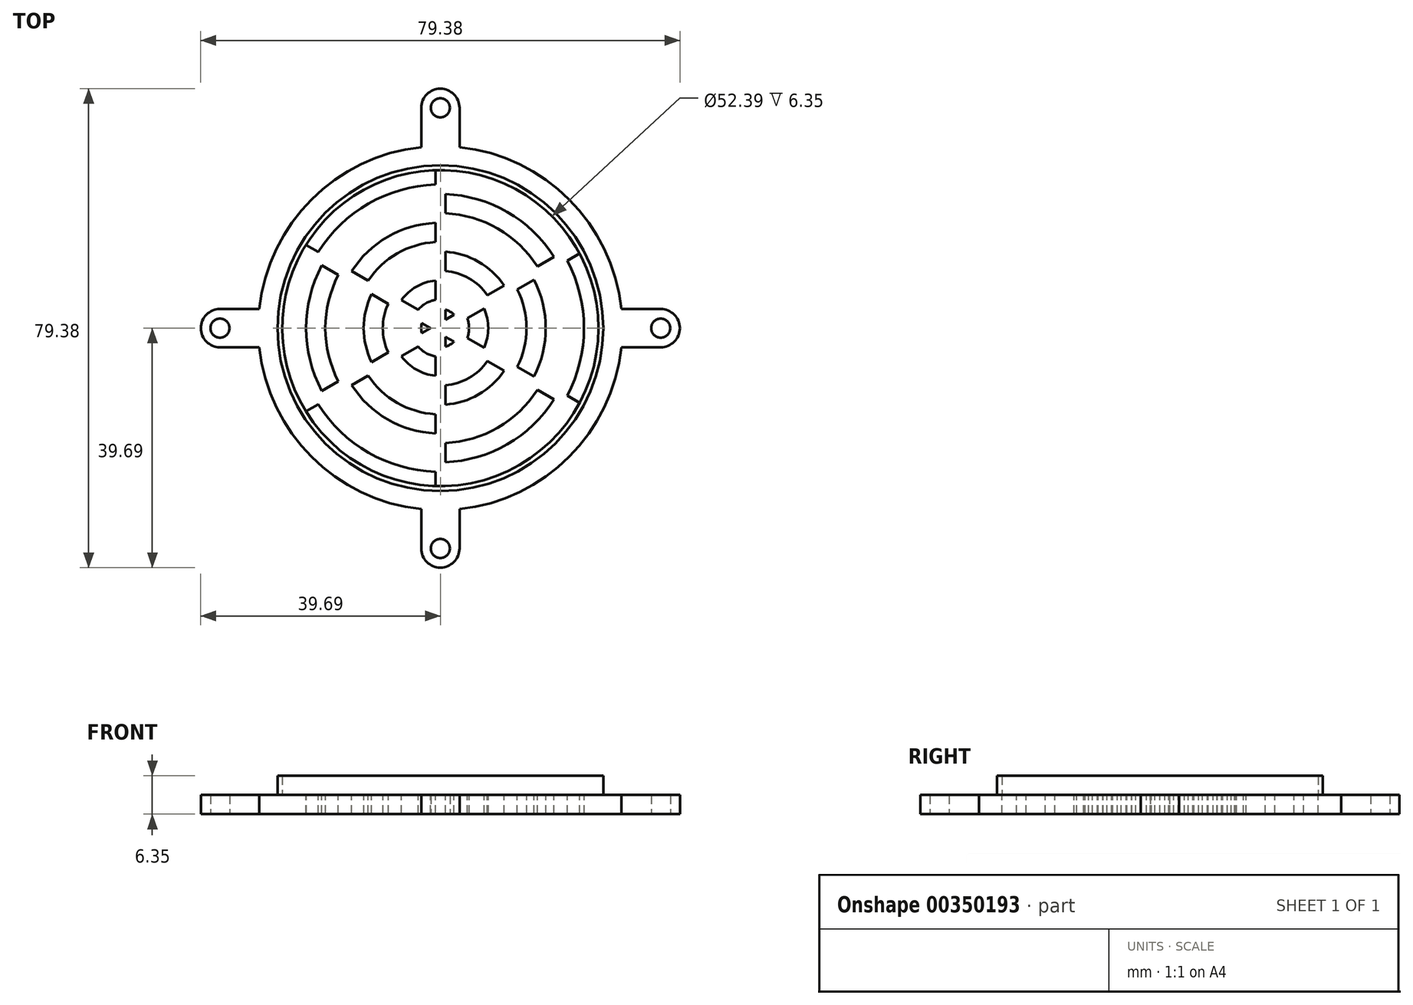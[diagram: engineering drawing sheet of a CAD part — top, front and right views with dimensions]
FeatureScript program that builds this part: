
annotation { "Feature Type Name" : "Feature", "Feature Type Description" : "" }
export const myFeature = defineFeature(function(context is Context, id is Id, definition is map)
    precondition{}
    {
        {
            var Q0;
            Q0=qCreatedBy(makeId("Top.planeOp"),FACE);
            var sketch = newSketch(context, id + "F0", { "sketchPlane" : qUnion([Q0])});
            skArc(sketch, "E0", {"start": v(30, 3.17) * mm, "mid": v(21.33, 21.33) * mm, "end": v(3.17, 30) * mm});
            skLineSegment(sketch, "E1.0", {"start": v(36.51, 3.18) * mm, "end": v(30, 3.17) * mm});
            skLineSegment(sketch, "E2.0", {"start": v(36.51, -3.17) * mm, "end": v(30, -3.17) * mm});
            skLineSegment(sketch, "E3.trimOffspring", {"start": v(-30, 3.17) * mm, "end": v(-30.16, 3.17) * mm});
            skArc(sketch, "E4", {"start": v(36.51, -3.17) * mm, "mid": v(39.69, 0) * mm, "end": v(36.51, 3.17) * mm});
            skCircle(sketch, "E5", {"center": v(36.51, 0) * mm, "radius": 1.59 * mm});
            skPoint(sketch, "E6.orphan", {"position": v(30.16, 0) * mm});
            skLineSegment(sketch, "E7.trimOffspring", {"start": v(-30, -3.18) * mm, "end": v(-30.16, -3.18) * mm});
            skLineSegment(sketch, "E8.1.0", {"start": v(-3.17, 36.51) * mm, "end": v(-3.17, 30) * mm});
            skArc(sketch, "E8.1.1", {"start": v(3.17, 36.51) * mm, "mid": v(0, 39.69) * mm, "end": v(-3.17, 36.51) * mm});
            skLineSegment(sketch, "E8.1.2", {"start": v(3.17, 36.51) * mm, "end": v(3.17, 30) * mm});
            skCircle(sketch, "E8.1.3", {"center": v(0, 36.51) * mm, "radius": 1.59 * mm});
            skLineSegment(sketch, "E8.2.0", {"start": v(-36.51, -3.17) * mm, "end": v(-30, -3.17) * mm});
            skArc(sketch, "E8.2.1", {"start": v(-36.51, 3.17) * mm, "mid": v(-39.69, 0) * mm, "end": v(-36.51, -3.17) * mm});
            skLineSegment(sketch, "E8.2.2", {"start": v(-36.51, 3.17) * mm, "end": v(-30, 3.17) * mm});
            skCircle(sketch, "E8.2.3", {"center": v(-36.51, 0) * mm, "radius": 1.59 * mm});
            skLineSegment(sketch, "E8.3.0", {"start": v(3.17, -36.51) * mm, "end": v(3.17, -30) * mm});
            skArc(sketch, "E8.3.1", {"start": v(-3.18, -36.51) * mm, "mid": v(0, -39.69) * mm, "end": v(3.17, -36.51) * mm});
            skLineSegment(sketch, "E8.3.2", {"start": v(-3.18, -36.51) * mm, "end": v(-3.18, -30) * mm});
            skCircle(sketch, "E8.3.3", {"center": v(0, -36.51) * mm, "radius": 1.59 * mm});
            skArc(sketch, "E9.trimOffspring", {"start": v(-3.17, 30) * mm, "mid": v(-21.33, 21.33) * mm, "end": v(-30, 3.17) * mm});
            skArc(sketch, "E10.trimOffspring", {"start": v(-30, -3.18) * mm, "mid": v(-21.33, -21.33) * mm, "end": v(-3.18, -30) * mm});
            skArc(sketch, "E11.trimOffspring", {"start": v(3.17, -30) * mm, "mid": v(21.33, -21.33) * mm, "end": v(30, -3.18) * mm});
            skSolve(sketch);
        }
        {
            var Q0;
            Q0=makeQuery(id+"F0.imprint","IMPRINT",FACE,{"disambiguationData":[TD([[makeQuery(id+"F0.imprint","IMPRINT",EDGE,{"derivedFrom":sQuery(id+"F0.wireOp",EDGE,"E0")}),1.0]])]});
            extrude(context, id + "F1", {"entities" : qUnion([Q0]), "depth" : 3.17 * mm});
        }
        {
            var Q0;
            Q0=makeQuery(id+"F1.opExtrude","CAP_FACE",FACE,{"disambiguationData":[OSD([sQuery(id+"F0.wireOp",EDGE,"E0"),sQuery(id+"F0.wireOp",EDGE,"E1.0"),sQuery(id+"F0.wireOp",EDGE,"E2.0"),sQuery(id+"F0.wireOp",EDGE,"E4"),sQuery(id+"F0.wireOp",EDGE,"E5"),sQuery(id+"F0.wireOp",EDGE,"E8.1.0"),sQuery(id+"F0.wireOp",EDGE,"E8.1.1"),sQuery(id+"F0.wireOp",EDGE,"E8.1.2"),sQuery(id+"F0.wireOp",EDGE,"E8.1.3"),sQuery(id+"F0.wireOp",EDGE,"E8.2.0"),sQuery(id+"F0.wireOp",EDGE,"E8.2.1"),sQuery(id+"F0.wireOp",EDGE,"E8.2.2"),sQuery(id+"F0.wireOp",EDGE,"E8.2.3"),sQuery(id+"F0.wireOp",EDGE,"E8.3.0"),sQuery(id+"F0.wireOp",EDGE,"E8.3.1"),sQuery(id+"F0.wireOp",EDGE,"E8.3.2"),sQuery(id+"F0.wireOp",EDGE,"E8.3.3"),sQuery(id+"F0.wireOp",EDGE,"E9.trimOffspring"),sQuery(id+"F0.wireOp",EDGE,"E10.trimOffspring"),sQuery(id+"F0.wireOp",EDGE,"E11.trimOffspring")])],"isStart":false});
            var sketch = newSketch(context, id + "F2", { "sketchPlane" : qUnion([Q0])});
            skCircle(sketch, "E12", {"center": v(0, 0) * mm, "radius": 26.99 * mm});
            skCircle(sketch, "E13", {"center": v(0, 0) * mm, "radius": 26.2 * mm});
            skSolve(sketch);
        }
        {
            var Q0;
            Q0=makeQuery(id+"F2.imprint","IMPRINT",FACE,{"disambiguationData":[TD([[makeQuery(id+"F2.imprint","IMPRINT",EDGE,{"derivedFrom":sQuery(id+"F2.wireOp",EDGE,"E12")}),1.0]])]});
            extrude(context, id + "F3", {"entities" : qUnion([Q0]), "operationType" : NewBodyOperationType.ADD, "depth" : 3.17 * mm});
        }
        {
            var Q0;
            Q0=makeQuery(id+"F3.boolean.opBoolean","SPLIT",FACE,{"disambiguationData":[TD([makeQuery(id+"F3.opExtrude","SWEPT_FACE",FACE,{"disambiguationData":[OSD([sQuery(id+"F2.wireOp",EDGE,"E13")])]})])],"derivedFrom":makeQuery(id+"F1.opExtrude","CAP_FACE",FACE,{"disambiguationData":[OSD([sQuery(id+"F0.wireOp",EDGE,"E0"),sQuery(id+"F0.wireOp",EDGE,"E1.0"),sQuery(id+"F0.wireOp",EDGE,"E2.0"),sQuery(id+"F0.wireOp",EDGE,"E4"),sQuery(id+"F0.wireOp",EDGE,"E5"),sQuery(id+"F0.wireOp",EDGE,"E8.1.0"),sQuery(id+"F0.wireOp",EDGE,"E8.1.1"),sQuery(id+"F0.wireOp",EDGE,"E8.1.2"),sQuery(id+"F0.wireOp",EDGE,"E8.1.3"),sQuery(id+"F0.wireOp",EDGE,"E8.2.0"),sQuery(id+"F0.wireOp",EDGE,"E8.2.1"),sQuery(id+"F0.wireOp",EDGE,"E8.2.2"),sQuery(id+"F0.wireOp",EDGE,"E8.2.3"),sQuery(id+"F0.wireOp",EDGE,"E8.3.0"),sQuery(id+"F0.wireOp",EDGE,"E8.3.1"),sQuery(id+"F0.wireOp",EDGE,"E8.3.2"),sQuery(id+"F0.wireOp",EDGE,"E8.3.3"),sQuery(id+"F0.wireOp",EDGE,"E9.trimOffspring"),sQuery(id+"F0.wireOp",EDGE,"E10.trimOffspring"),sQuery(id+"F0.wireOp",EDGE,"E11.trimOffspring")])],"isStart":false})});
            var sketch = newSketch(context, id + "F4", { "sketchPlane" : qUnion([Q0])});
            skArc(sketch, "E14", {"start": v(0.83, -3.07) * mm, "mid": v(1.59, -2.75) * mm, "end": v(2.24, -2.25) * mm});
            skArc(sketch, "E15", {"start": v(0.83, -4.7) * mm, "mid": v(2.38, -4.12) * mm, "end": v(3.65, -3.06) * mm});
            skArc(sketch, "E16", {"start": v(0.83, -7.9) * mm, "mid": v(3.97, -6.87) * mm, "end": v(6.42, -4.66) * mm});
            skArc(sketch, "E17", {"start": v(0.83, -9.49) * mm, "mid": v(4.76, -8.25) * mm, "end": v(7.8, -5.46) * mm});
            skArc(sketch, "E18", {"start": v(0.83, -12.67) * mm, "mid": v(6.35, -11) * mm, "end": v(10.56, -7.05) * mm});
            skArc(sketch, "E19", {"start": v(0.83, -14.26) * mm, "mid": v(7.14, -12.37) * mm, "end": v(11.94, -7.85) * mm});
            skArc(sketch, "E20", {"start": v(0.83, -17.44) * mm, "mid": v(8.73, -15.12) * mm, "end": v(14.7, -9.44) * mm});
            skArc(sketch, "E21", {"start": v(0.83, -19.03) * mm, "mid": v(9.52, -16.5) * mm, "end": v(16.07, -10.23) * mm});
            skArc(sketch, "E22", {"start": v(0.83, -22.2) * mm, "mid": v(11.11, -19.25) * mm, "end": v(18.82, -11.82) * mm});
            skArc(sketch, "E23", {"start": v(0.83, -23.8) * mm, "mid": v(11.9, -20.62) * mm, "end": v(20.2, -12.61) * mm});
            skLineSegment(sketch, "E24.0", {"start": v(0.83, -1.43) * mm, "end": v(0.83, -3.07) * mm});
            skLineSegment(sketch, "E25.1.0", {"start": v(0.83, -1.43) * mm, "end": v(2.24, -2.25) * mm});
            skLineSegment(sketch, "E25.1.1", {"start": v(1.65, 0) * mm, "end": v(3.07, -0.82) * mm});
            skLineSegment(sketch, "E25.5.1", {"start": v(-0.83, -1.43) * mm, "end": v(-2.24, -2.25) * mm});
            skArc(sketch, "E26.trimOffspring", {"start": v(21.02, -11.18) * mm, "mid": v(23.81, 0) * mm, "end": v(21.02, 11.18) * mm});
            skArc(sketch, "E27.trimOffspring", {"start": v(19.65, -10.39) * mm, "mid": v(22.23, 0) * mm, "end": v(19.65, 10.39) * mm});
            skArc(sketch, "E28.trimOffspring", {"start": v(16.9, -8.8) * mm, "mid": v(19.05, 0) * mm, "end": v(16.9, 8.8) * mm});
            skArc(sketch, "E29.trimOffspring", {"start": v(15.52, -8) * mm, "mid": v(17.46, 0) * mm, "end": v(15.52, 8) * mm});
            skArc(sketch, "E30.trimOffspring", {"start": v(12.77, -6.42) * mm, "mid": v(14.29, 0) * mm, "end": v(12.77, 6.42) * mm});
            skArc(sketch, "E31.trimOffspring", {"start": v(11.39, -5.62) * mm, "mid": v(12.7, 0) * mm, "end": v(11.39, 5.62) * mm});
            skArc(sketch, "E32.trimOffspring", {"start": v(8.63, -4.03) * mm, "mid": v(9.53, 0) * mm, "end": v(8.63, 4.03) * mm});
            skArc(sketch, "E33.trimOffspring", {"start": v(7.25, -3.23) * mm, "mid": v(7.94, 0) * mm, "end": v(7.25, 3.23) * mm});
            skArc(sketch, "E34.trimOffspring", {"start": v(4.47, -1.63) * mm, "mid": v(4.76, 0) * mm, "end": v(4.47, 1.63) * mm});
            skArc(sketch, "E35.trimOffspring", {"start": v(3.07, -0.82) * mm, "mid": v(3.18, 0) * mm, "end": v(3.07, 0.82) * mm});
            skArc(sketch, "E36.trimOffspring", {"start": v(-2.24, -2.25) * mm, "mid": v(-1.59, -2.75) * mm, "end": v(-0.83, -3.07) * mm});
            skArc(sketch, "E37.trimOffspring", {"start": v(-3.65, -3.06) * mm, "mid": v(-2.38, -4.12) * mm, "end": v(-0.83, -4.7) * mm});
            skArc(sketch, "E38.trimOffspring", {"start": v(-6.42, -4.66) * mm, "mid": v(-3.97, -6.87) * mm, "end": v(-0.83, -7.9) * mm});
            skArc(sketch, "E39.trimOffspring", {"start": v(-7.8, -5.46) * mm, "mid": v(-4.76, -8.25) * mm, "end": v(-0.83, -9.49) * mm});
            skArc(sketch, "E40.trimOffspring", {"start": v(-10.56, -7.05) * mm, "mid": v(-6.35, -11) * mm, "end": v(-0.83, -12.67) * mm});
            skArc(sketch, "E41.trimOffspring", {"start": v(-11.94, -7.85) * mm, "mid": v(-7.14, -12.37) * mm, "end": v(-0.83, -14.26) * mm});
            skArc(sketch, "E42.trimOffspring", {"start": v(-14.7, -9.44) * mm, "mid": v(-8.73, -15.12) * mm, "end": v(-0.83, -17.44) * mm});
            skArc(sketch, "E43.trimOffspring", {"start": v(-16.07, -10.23) * mm, "mid": v(-9.53, -16.5) * mm, "end": v(-0.83, -19.03) * mm});
            skArc(sketch, "E44.trimOffspring", {"start": v(-18.82, -11.82) * mm, "mid": v(-11.11, -19.25) * mm, "end": v(-0.83, -22.2) * mm});
            skArc(sketch, "E45.trimOffspring", {"start": v(-20.2, -12.61) * mm, "mid": v(-11.9, -20.62) * mm, "end": v(-0.83, -23.8) * mm});
            skArc(sketch, "E46.trimOffspring", {"start": v(-3.07, 0.82) * mm, "mid": v(-3.18, 0) * mm, "end": v(-3.07, -0.82) * mm});
            skArc(sketch, "E47.trimOffspring", {"start": v(-4.47, 1.63) * mm, "mid": v(-4.76, 0) * mm, "end": v(-4.47, -1.63) * mm});
            skArc(sketch, "E48.trimOffspring", {"start": v(-7.25, 3.23) * mm, "mid": v(-7.94, 0) * mm, "end": v(-7.25, -3.23) * mm});
            skArc(sketch, "E49.trimOffspring", {"start": v(-8.63, 4.03) * mm, "mid": v(-9.53, 0) * mm, "end": v(-8.63, -4.03) * mm});
            skArc(sketch, "E50.trimOffspring", {"start": v(-11.39, 5.62) * mm, "mid": v(-12.7, 0) * mm, "end": v(-11.39, -5.62) * mm});
            skArc(sketch, "E51.trimOffspring", {"start": v(-12.77, 6.42) * mm, "mid": v(-14.29, 0) * mm, "end": v(-12.77, -6.42) * mm});
            skArc(sketch, "E52.trimOffspring", {"start": v(-15.52, 8) * mm, "mid": v(-17.46, 0) * mm, "end": v(-15.52, -8) * mm});
            skArc(sketch, "E53.trimOffspring", {"start": v(-16.9, 8.8) * mm, "mid": v(-19.05, 0) * mm, "end": v(-16.9, -8.8) * mm});
            skArc(sketch, "E54.trimOffspring", {"start": v(-19.65, 10.39) * mm, "mid": v(-22.22, 0) * mm, "end": v(-19.65, -10.39) * mm});
            skArc(sketch, "E55.trimOffspring", {"start": v(-21.02, 11.18) * mm, "mid": v(-23.81, 0) * mm, "end": v(-21.02, -11.18) * mm});
            skArc(sketch, "E56.trimOffspring", {"start": v(2.24, 2.25) * mm, "mid": v(1.59, 2.75) * mm, "end": v(0.83, 3.07) * mm});
            skArc(sketch, "E57.trimOffspring", {"start": v(3.65, 3.06) * mm, "mid": v(2.38, 4.12) * mm, "end": v(0.83, 4.7) * mm});
            skArc(sketch, "E58.trimOffspring", {"start": v(6.42, 4.66) * mm, "mid": v(3.97, 6.87) * mm, "end": v(0.83, 7.9) * mm});
            skArc(sketch, "E59.trimOffspring", {"start": v(7.8, 5.46) * mm, "mid": v(4.76, 8.25) * mm, "end": v(0.83, 9.49) * mm});
            skArc(sketch, "E60.trimOffspring", {"start": v(10.56, 7.05) * mm, "mid": v(6.35, 11) * mm, "end": v(0.83, 12.67) * mm});
            skArc(sketch, "E61.trimOffspring", {"start": v(11.94, 7.85) * mm, "mid": v(7.14, 12.37) * mm, "end": v(0.83, 14.26) * mm});
            skArc(sketch, "E62.trimOffspring", {"start": v(14.7, 9.44) * mm, "mid": v(8.73, 15.12) * mm, "end": v(0.83, 17.44) * mm});
            skArc(sketch, "E63.trimOffspring", {"start": v(16.07, 10.23) * mm, "mid": v(9.53, 16.5) * mm, "end": v(0.83, 19.03) * mm});
            skArc(sketch, "E64.trimOffspring", {"start": v(18.82, 11.82) * mm, "mid": v(11.11, 19.25) * mm, "end": v(0.83, 22.2) * mm});
            skArc(sketch, "E65.trimOffspring", {"start": v(20.2, 12.61) * mm, "mid": v(11.9, 20.62) * mm, "end": v(0.83, 23.8) * mm});
            skArc(sketch, "E66.trimOffspring", {"start": v(-0.83, 4.7) * mm, "mid": v(-2.38, 4.12) * mm, "end": v(-3.65, 3.06) * mm});
            skArc(sketch, "E67.trimOffspring", {"start": v(-0.83, 3.07) * mm, "mid": v(-1.59, 2.75) * mm, "end": v(-2.24, 2.25) * mm});
            skArc(sketch, "E68.trimOffspring", {"start": v(-0.83, 7.9) * mm, "mid": v(-3.97, 6.87) * mm, "end": v(-6.42, 4.66) * mm});
            skLineSegment(sketch, "E69.trimOffspring", {"start": v(0.83, 1.43) * mm, "end": v(0.83, 3.07) * mm});
            skLineSegment(sketch, "E70.trimOffspring", {"start": v(0.83, 1.43) * mm, "end": v(2.24, 2.25) * mm});
            skLineSegment(sketch, "E71.trimOffspring", {"start": v(-0.83, 1.43) * mm, "end": v(-2.24, 2.25) * mm});
            skLineSegment(sketch, "E72.trimOffspring", {"start": v(-0.83, 1.43) * mm, "end": v(-0.83, 3.07) * mm});
            skLineSegment(sketch, "E73.trimOffspring", {"start": v(-1.65, 0) * mm, "end": v(-3.07, -0.82) * mm});
            skLineSegment(sketch, "E74.trimOffspring", {"start": v(-1.65, 0) * mm, "end": v(-3.07, 0.82) * mm});
            skLineSegment(sketch, "E75.trimOffspring", {"start": v(-0.83, -1.43) * mm, "end": v(-0.83, -3.07) * mm});
            skPoint(sketch, "E76.orphan", {"position": v(0.41, 0.71) * mm});
            skLineSegment(sketch, "E77.trimOffspring", {"start": v(1.65, 0) * mm, "end": v(3.07, 0.82) * mm});
            skPoint(sketch, "E78.orphan", {"position": v(0.83, 0) * mm});
            skPoint(sketch, "E79.orphan", {"position": v(0.41, -0.71) * mm});
            skPoint(sketch, "E80.orphan", {"position": v(-0.41, -0.71) * mm});
            skArc(sketch, "E81.trimOffspring", {"start": v(-0.83, 9.49) * mm, "mid": v(-4.76, 8.25) * mm, "end": v(-7.8, 5.46) * mm});
            skArc(sketch, "E82.trimOffspring", {"start": v(-0.83, 12.67) * mm, "mid": v(-6.35, 11) * mm, "end": v(-10.56, 7.05) * mm});
            skArc(sketch, "E83.trimOffspring", {"start": v(-0.83, 14.26) * mm, "mid": v(-7.14, 12.37) * mm, "end": v(-11.94, 7.85) * mm});
            skArc(sketch, "E84.trimOffspring", {"start": v(-0.83, 17.44) * mm, "mid": v(-8.73, 15.12) * mm, "end": v(-14.7, 9.44) * mm});
            skArc(sketch, "E85.trimOffspring", {"start": v(-0.83, 19.03) * mm, "mid": v(-9.52, 16.5) * mm, "end": v(-16.07, 10.23) * mm});
            skArc(sketch, "E86.trimOffspring", {"start": v(-0.83, 22.2) * mm, "mid": v(-11.11, 19.25) * mm, "end": v(-18.82, 11.82) * mm});
            skArc(sketch, "E87.trimOffspring", {"start": v(-0.83, 23.8) * mm, "mid": v(-11.9, 20.62) * mm, "end": v(-20.2, 12.61) * mm});
            skLineSegment(sketch, "E88.trimOffspring", {"start": v(3.65, 3.06) * mm, "end": v(6.42, 4.66) * mm});
            skLineSegment(sketch, "E89.trimOffspring", {"start": v(4.47, 1.63) * mm, "end": v(7.25, 3.23) * mm});
            skLineSegment(sketch, "E90.trimOffspring", {"start": v(4.47, -1.63) * mm, "end": v(7.25, -3.23) * mm});
            skLineSegment(sketch, "E91.trimOffspring", {"start": v(3.65, -3.06) * mm, "end": v(6.42, -4.66) * mm});
            skLineSegment(sketch, "E92.trimOffspring", {"start": v(0.83, -4.7) * mm, "end": v(0.83, -7.9) * mm});
            skLineSegment(sketch, "E93.trimOffspring", {"start": v(-0.83, -4.7) * mm, "end": v(-0.83, -7.9) * mm});
            skLineSegment(sketch, "E94.trimOffspring", {"start": v(-3.65, -3.06) * mm, "end": v(-10.56, -7.05) * mm});
            skLineSegment(sketch, "E95.trimOffspring", {"start": v(-4.47, -1.63) * mm, "end": v(-7.25, -3.23) * mm});
            skLineSegment(sketch, "E96.trimOffspring", {"start": v(-4.47, 1.63) * mm, "end": v(-7.25, 3.23) * mm});
            skLineSegment(sketch, "E97.trimOffspring", {"start": v(-3.65, 3.06) * mm, "end": v(-6.42, 4.66) * mm});
            skLineSegment(sketch, "E98.trimOffspring", {"start": v(-0.83, 4.7) * mm, "end": v(-0.83, 7.9) * mm});
            skLineSegment(sketch, "E99.trimOffspring", {"start": v(0.83, 4.7) * mm, "end": v(0.83, 7.9) * mm});
            skLineSegment(sketch, "E100.trimOffspring", {"start": v(0.83, 9.49) * mm, "end": v(0.83, 12.67) * mm});
            skLineSegment(sketch, "E101.trimOffspring", {"start": v(-0.83, 9.49) * mm, "end": v(-0.83, 12.67) * mm});
            skLineSegment(sketch, "E102.trimOffspring", {"start": v(-7.8, 5.46) * mm, "end": v(-10.56, 7.05) * mm});
            skLineSegment(sketch, "E103.trimOffspring", {"start": v(-8.63, 4.03) * mm, "end": v(-11.39, 5.62) * mm});
            skLineSegment(sketch, "E104.trimOffspring", {"start": v(-8.63, -4.03) * mm, "end": v(-11.39, -5.62) * mm});
            skLineSegment(sketch, "E105.trimOffspring", {"start": v(0.83, 14.26) * mm, "end": v(0.83, 17.44) * mm});
            skLineSegment(sketch, "E106.trimOffspring", {"start": v(-0.83, 14.26) * mm, "end": v(-0.83, 17.44) * mm});
            skLineSegment(sketch, "E107.trimOffspring", {"start": v(-0.83, 19.03) * mm, "end": v(-0.83, 22.2) * mm});
            skLineSegment(sketch, "E108.trimOffspring", {"start": v(0.83, 19.03) * mm, "end": v(0.83, 22.2) * mm});
            skLineSegment(sketch, "E109.trimOffspring", {"start": v(-0.83, 23.8) * mm, "end": v(-0.83, 26.2) * mm});
            skLineSegment(sketch, "E110.trimOffspring", {"start": v(0.83, 23.8) * mm, "end": v(0.83, 26.2) * mm});
            skLineSegment(sketch, "E111.trimOffspring", {"start": v(7.8, 5.46) * mm, "end": v(10.56, 7.05) * mm});
            skLineSegment(sketch, "E112.trimOffspring", {"start": v(8.63, 4.03) * mm, "end": v(11.39, 5.62) * mm});
            skLineSegment(sketch, "E113.trimOffspring", {"start": v(11.94, 7.85) * mm, "end": v(14.7, 9.44) * mm});
            skLineSegment(sketch, "E114.trimOffspring", {"start": v(12.77, 6.42) * mm, "end": v(15.52, 8) * mm});
            skLineSegment(sketch, "E115.trimOffspring", {"start": v(16.07, 10.23) * mm, "end": v(18.82, 11.82) * mm});
            skLineSegment(sketch, "E116.trimOffspring", {"start": v(16.9, 8.8) * mm, "end": v(19.65, 10.39) * mm});
            skLineSegment(sketch, "E117.trimOffspring", {"start": v(20.2, 12.61) * mm, "end": v(22.27, 13.81) * mm});
            skLineSegment(sketch, "E118.trimOffspring", {"start": v(21.02, 11.18) * mm, "end": v(23.1, 12.38) * mm});
            skLineSegment(sketch, "E119.trimOffspring", {"start": v(21.02, -11.18) * mm, "end": v(23.1, -12.38) * mm});
            skLineSegment(sketch, "E120.trimOffspring", {"start": v(20.2, -12.61) * mm, "end": v(22.27, -13.81) * mm});
            skLineSegment(sketch, "E121.trimOffspring", {"start": v(16.9, -8.8) * mm, "end": v(19.65, -10.39) * mm});
            skLineSegment(sketch, "E122.trimOffspring", {"start": v(16.07, -10.23) * mm, "end": v(18.82, -11.82) * mm});
            skLineSegment(sketch, "E123.trimOffspring", {"start": v(11.94, -7.85) * mm, "end": v(14.7, -9.44) * mm});
            skLineSegment(sketch, "E124.trimOffspring", {"start": v(12.77, -6.42) * mm, "end": v(15.52, -8) * mm});
            skLineSegment(sketch, "E125.trimOffspring", {"start": v(7.8, -5.46) * mm, "end": v(10.56, -7.05) * mm});
            skLineSegment(sketch, "E126.trimOffspring", {"start": v(8.63, -4.03) * mm, "end": v(11.39, -5.62) * mm});
            skLineSegment(sketch, "E127.trimOffspring", {"start": v(-11.94, -7.85) * mm, "end": v(-14.7, -9.44) * mm});
            skLineSegment(sketch, "E128.trimOffspring", {"start": v(-12.77, -6.42) * mm, "end": v(-15.52, -8) * mm});
            skLineSegment(sketch, "E129.trimOffspring", {"start": v(-16.07, -10.23) * mm, "end": v(-18.82, -11.82) * mm});
            skLineSegment(sketch, "E130.trimOffspring", {"start": v(-16.9, -8.8) * mm, "end": v(-19.65, -10.39) * mm});
            skLineSegment(sketch, "E131.trimOffspring", {"start": v(-20.2, -12.61) * mm, "end": v(-22.27, -13.81) * mm});
            skLineSegment(sketch, "E132.trimOffspring", {"start": v(-21.02, -11.18) * mm, "end": v(-23.1, -12.38) * mm});
            skLineSegment(sketch, "E133.trimOffspring", {"start": v(-0.83, -23.8) * mm, "end": v(-0.83, -26.2) * mm});
            skLineSegment(sketch, "E134.trimOffspring", {"start": v(0.83, -23.8) * mm, "end": v(0.83, -26.2) * mm});
            skLineSegment(sketch, "E135.trimOffspring", {"start": v(-0.83, -19.03) * mm, "end": v(-0.83, -22.2) * mm});
            skLineSegment(sketch, "E136.trimOffspring", {"start": v(0.83, -19.03) * mm, "end": v(0.83, -22.2) * mm});
            skLineSegment(sketch, "E137.trimOffspring", {"start": v(0.83, -14.26) * mm, "end": v(0.83, -17.44) * mm});
            skLineSegment(sketch, "E138.trimOffspring", {"start": v(-0.83, -14.26) * mm, "end": v(-0.83, -17.44) * mm});
            skLineSegment(sketch, "E139.trimOffspring", {"start": v(0.83, -9.49) * mm, "end": v(0.83, -12.67) * mm});
            skLineSegment(sketch, "E140.trimOffspring", {"start": v(-0.83, -9.49) * mm, "end": v(-0.83, -12.67) * mm});
            skLineSegment(sketch, "E141.trimOffspring", {"start": v(-11.94, 7.85) * mm, "end": v(-14.7, 9.44) * mm});
            skLineSegment(sketch, "E142.trimOffspring", {"start": v(-16.07, 10.23) * mm, "end": v(-18.82, 11.82) * mm});
            skLineSegment(sketch, "E143.trimOffspring", {"start": v(-20.2, 12.61) * mm, "end": v(-22.27, 13.81) * mm});
            skLineSegment(sketch, "E144.trimOffspring", {"start": v(-21.02, 11.18) * mm, "end": v(-23.1, 12.38) * mm});
            skLineSegment(sketch, "E145.trimOffspring", {"start": v(-16.9, 8.8) * mm, "end": v(-19.65, 10.39) * mm});
            skLineSegment(sketch, "E146.trimOffspring", {"start": v(-12.77, 6.42) * mm, "end": v(-15.52, 8) * mm});
            skSolve(sketch);
        }
        {
            var Q0;
            {var subQ0=sQuery(id+"F4.wireOp",EDGE,"E87.trimOffspring");Q0=makeQuery(id+"F4.imprint","IMPRINT",FACE,{"disambiguationData":[TD([[makeQuery(id+"F4.imprint","IMPRINT",EDGE,{"derivedFrom":subQ0}),-1.0]])]});}
            var Q1;
            Q1=makeQuery(id+"F4.imprint","IMPRINT",FACE,{"disambiguationData":[TD([[makeQuery(id+"F4.imprint","IMPRINT",EDGE,{"derivedFrom":sQuery(id+"F4.wireOp",EDGE,"E63.trimOffspring")}),-1.0]])]});
            var Q2;
            {var subQ0=sQuery(id+"F4.wireOp",EDGE,"E26.trimOffspring");Q2=makeQuery(id+"F4.imprint","IMPRINT",FACE,{"disambiguationData":[TD([[makeQuery(id+"F4.imprint","IMPRINT",EDGE,{"derivedFrom":subQ0}),-1.0]])]});}
            var Q3;
            Q3=makeQuery(id+"F4.imprint","IMPRINT",FACE,{"disambiguationData":[TD([[makeQuery(id+"F4.imprint","IMPRINT",EDGE,{"derivedFrom":sQuery(id+"F4.wireOp",EDGE,"E29.trimOffspring")}),1.0]])]});
            var Q4;
            Q4=makeQuery(id+"F4.imprint","IMPRINT",FACE,{"disambiguationData":[TD([[makeQuery(id+"F4.imprint","IMPRINT",EDGE,{"derivedFrom":sQuery(id+"F4.wireOp",EDGE,"E33.trimOffspring")}),1.0]])]});
            var Q5;
            Q5=makeQuery(id+"F4.imprint","IMPRINT",FACE,{"disambiguationData":[TD([[makeQuery(id+"F4.imprint","IMPRINT",EDGE,{"derivedFrom":sQuery(id+"F4.wireOp",EDGE,"E59.trimOffspring")}),-1.0]])]});
            var Q6;
            Q6=makeQuery(id+"F4.imprint","IMPRINT",FACE,{"disambiguationData":[TD([[makeQuery(id+"F4.imprint","IMPRINT",EDGE,{"derivedFrom":sQuery(id+"F4.wireOp",EDGE,"E83.trimOffspring")}),-1.0]])]});
            var Q7;
            Q7=makeQuery(id+"F4.imprint","IMPRINT",FACE,{"disambiguationData":[TD([[makeQuery(id+"F4.imprint","IMPRINT",EDGE,{"derivedFrom":sQuery(id+"F4.wireOp",EDGE,"E53.trimOffspring")}),-1.0]])]});
            var Q8;
            Q8=makeQuery(id+"F4.imprint","IMPRINT",FACE,{"disambiguationData":[TD([[makeQuery(id+"F4.imprint","IMPRINT",EDGE,{"derivedFrom":sQuery(id+"F4.wireOp",EDGE,"E49.trimOffspring")}),-1.0]])]});
            var Q9;
            Q9=makeQuery(id+"F4.imprint","IMPRINT",FACE,{"disambiguationData":[TD([[makeQuery(id+"F4.imprint","IMPRINT",EDGE,{"derivedFrom":sQuery(id+"F4.wireOp",EDGE,"E41.trimOffspring")}),-1.0]])]});
            var Q10;
            {var subQ0=sQuery(id+"F4.wireOp",EDGE,"E45.trimOffspring");Q10=makeQuery(id+"F4.imprint","IMPRINT",FACE,{"disambiguationData":[TD([[makeQuery(id+"F4.imprint","IMPRINT",EDGE,{"derivedFrom":subQ0}),-1.0]])]});}
            var Q11;
            Q11=makeQuery(id+"F4.imprint","IMPRINT",FACE,{"disambiguationData":[TD([[makeQuery(id+"F4.imprint","IMPRINT",EDGE,{"derivedFrom":sQuery(id+"F4.wireOp",EDGE,"E21")}),-1.0]])]});
            var Q12;
            Q12=makeQuery(id+"F4.imprint","IMPRINT",FACE,{"disambiguationData":[TD([[makeQuery(id+"F4.imprint","IMPRINT",EDGE,{"derivedFrom":sQuery(id+"F4.wireOp",EDGE,"E17")}),-1.0]])]});
            var Q13;
            {var subQ0=sQuery(id+"F4.wireOp",EDGE,"E37.trimOffspring");Q13=makeQuery(id+"F4.imprint","IMPRINT",FACE,{"disambiguationData":[TD([[makeQuery(id+"F4.imprint","IMPRINT",EDGE,{"derivedFrom":subQ0}),-1.0]])]});}
            var Q14;
            Q14=makeQuery(id+"F4.imprint","IMPRINT",FACE,{"disambiguationData":[TD([[makeQuery(id+"F4.imprint","IMPRINT",EDGE,{"derivedFrom":sQuery(id+"F4.wireOp",EDGE,"E66.trimOffspring")}),-1.0]])]});
            var Q15;
            Q15=makeQuery(id+"F4.imprint","IMPRINT",FACE,{"disambiguationData":[TD([[makeQuery(id+"F4.imprint","IMPRINT",EDGE,{"derivedFrom":sQuery(id+"F4.wireOp",EDGE,"E56.trimOffspring")}),1.0]])]});
            var Q16;
            Q16=makeQuery(id+"F4.imprint","IMPRINT",FACE,{"disambiguationData":[TD([[makeQuery(id+"F4.imprint","IMPRINT",EDGE,{"derivedFrom":sQuery(id+"F4.wireOp",EDGE,"E14")}),1.0]])]});
            var Q17;
            Q17=makeQuery(id+"F4.imprint","IMPRINT",FACE,{"disambiguationData":[TD([[makeQuery(id+"F4.imprint","IMPRINT",EDGE,{"derivedFrom":sQuery(id+"F4.wireOp",EDGE,"E46.trimOffspring")}),1.0]])]});
            extrude(context, id + "F5", {"entities" : qUnion([Q0, Q1, Q2, Q3, Q4, Q5, Q6, Q7, Q8, Q9, Q10, Q11, Q12, Q13, Q14, Q15, Q16, Q17]), "operationType" : NewBodyOperationType.REMOVE, "oppositeDirection" : true, "depth" : 3.17 * mm});
        }
    });
